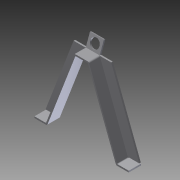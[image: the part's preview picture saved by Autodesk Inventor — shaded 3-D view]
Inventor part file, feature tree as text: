
AUTODESK INVENTOR PART (.ipt)
format: ipt  version: 2012 (Build 160160000, 160)  size: 155,648 bytes
history: native  units: in
note: dims shown in document units (in); Inventor stores cm internally (conversion verified against a paired STEP export)
features: extrude x4, sketch x3, fillet x3, plane x1
ambient origin geometry x8: Origin, YZ Plane, XZ Plane, XY Plane, X Axis, Y Axis, Z Axis, Center Point
bodies: Solid1 (feature_tree)
feature tree (11):
  sketch  "Sketch1"  dims[d0=7.625in d1=1.0in]
  extrude  "Extrusion1"  Depth=1.0in
  extrude  "Extrusion2"  Depth=1.0in
  fillet  "Fillet1"  Radius=0.125in
  fillet  "Fillet2"  Radius=0.125in
  plane  "Work Plane1"
  extrude  "Extrusion3"  Depth=0.0625in
  fillet  "Fillet3"  Radius=0.0625in
  extrude  "Extrusion4"  Depth=0.0625in
  sketch  "Sketch2"  dims[d2=1.0in d3=1.0in d4=0.125in d5=0.125in]
  sketch  "Sketch3"  dims[d6=6.0in d7=0.0625in d8=0.0625in d9=0.0625in d10=1.0in d11=0.0in d12=0.125in d13=0.0in d14=0.0625in d15=0.125in d16=0.125in d17=0.7559in d18=1.0in d19=0.1in d20=1.125in d21=0.0in d22=0.125in d23=0.75in d24=0.5625in d25=0.5in d26=1.0in d27=0.0in]
